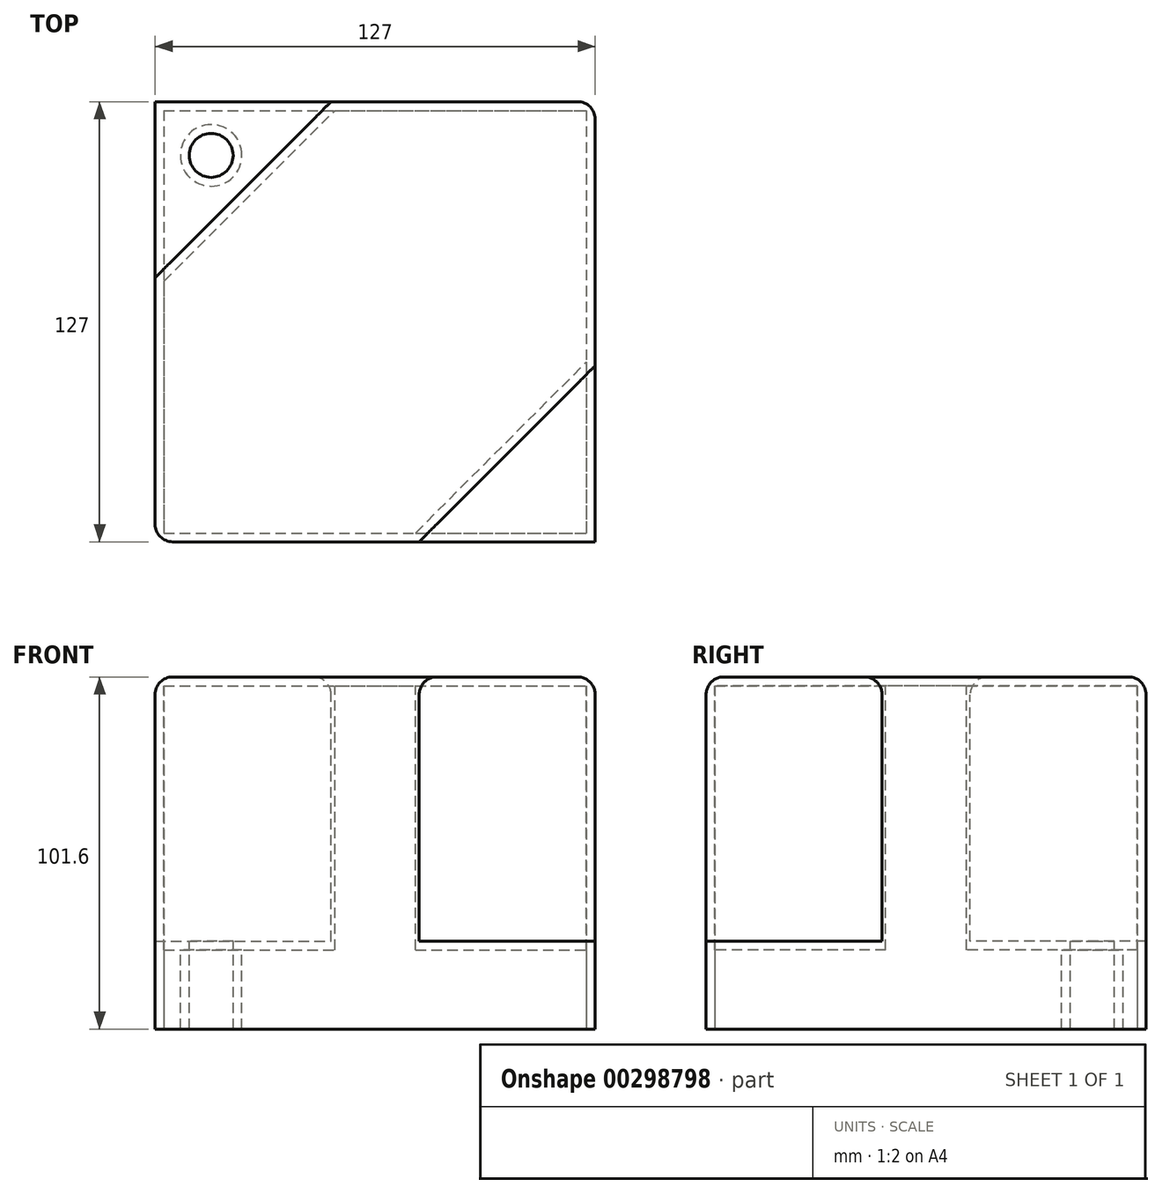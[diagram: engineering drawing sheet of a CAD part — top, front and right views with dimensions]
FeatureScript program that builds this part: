
annotation { "Feature Type Name" : "Feature", "Feature Type Description" : "" }
export const myFeature = defineFeature(function(context is Context, id is Id, definition is map)
    precondition{}
    {
        {
            var Q0;
            Q0=qCreatedBy(makeId("Top.planeOp"),FACE);
            var sketch = newSketch(context, id + "F0", { "sketchPlane" : qUnion([Q0])});
            skLineSegment(sketch, "E0.bottom", {"start": v(-63.5, 63.5) * mm, "end": v(63.5, 63.5) * mm});
            skLineSegment(sketch, "E0.top", {"start": v(-63.5, -63.5) * mm, "end": v(63.5, -63.5) * mm});
            skLineSegment(sketch, "E0.left", {"start": v(-63.5, 63.5) * mm, "end": v(-63.5, -63.5) * mm});
            skLineSegment(sketch, "E0.right", {"start": v(63.5, 63.5) * mm, "end": v(63.5, -63.5) * mm});
            skPoint(sketch, "E0.middle", {"position": v(0, 0) * mm});
            skSolve(sketch);
        }
        {
            var Q0;
            Q0=makeQuery(id+"F0.imprint","IMPRINT",FACE,{"disambiguationData":[TD([[makeQuery(id+"F0.imprint","IMPRINT",EDGE,{"derivedFrom":sQuery(id+"F0.wireOp",EDGE,"E0.bottom")}),-1.0]])]});
            extrude(context, id + "F1", {"entities" : qUnion([Q0]), "depth" : 101.6 * mm});
        }
        {
            var Q0;
            Q0=makeQuery(id+"F1.opExtrude","CAP_FACE",FACE,{"disambiguationData":[OSD([sQuery(id+"F0.wireOp",EDGE,"E0.bottom"),sQuery(id+"F0.wireOp",EDGE,"E0.top"),sQuery(id+"F0.wireOp",EDGE,"E0.left"),sQuery(id+"F0.wireOp",EDGE,"E0.right")])],"isStart":false});
            var sketch = newSketch(context, id + "F2", { "sketchPlane" : qUnion([Q0])});
            skLineSegment(sketch, "E1", {"start": v(-12.7, 63.5) * mm, "end": v(-63.5, 63.5) * mm});
            skLineSegment(sketch, "E2", {"start": v(-63.5, 63.5) * mm, "end": v(-63.5, 12.7) * mm});
            skLineSegment(sketch, "E3", {"start": v(-63.5, 12.7) * mm, "end": v(-12.7, 63.5) * mm});
            skLineSegment(sketch, "E4", {"start": v(-63.5, -63.5) * mm, "end": v(63.5, 63.5) * mm, "construction": true});
            skLineSegment(sketch, "E5.MirrorCS", {"start": v(12.7, -63.5) * mm, "end": v(63.5, -12.7) * mm});
            skLineSegment(sketch, "E6.MirrorCS", {"start": v(63.5, -12.7) * mm, "end": v(63.5, -63.5) * mm});
            skLineSegment(sketch, "E7.MirrorCS", {"start": v(63.5, -63.5) * mm, "end": v(12.7, -63.5) * mm});
            skSolve(sketch);
        }
        {
            var Q0;
            Q0=makeQuery(id+"F2.imprint","IMPRINT",FACE,{"disambiguationData":[TD([[makeQuery(id+"F2.imprint","IMPRINT",EDGE,{"derivedFrom":sQuery(id+"F2.wireOp",EDGE,"E5.MirrorCS")}),-1.0]])]});
            var Q1;
            Q1=makeQuery(id+"F2.imprint","IMPRINT",FACE,{"disambiguationData":[TD([[makeQuery(id+"F2.imprint","IMPRINT",EDGE,{"derivedFrom":sQuery(id+"F2.wireOp",EDGE,"E1")}),-1.0]])]});
            extrude(context, id + "F3", {"entities" : qUnion([Q0, Q1]), "operationType" : NewBodyOperationType.REMOVE, "oppositeDirection" : true, "depth" : 76.2 * mm});
        }
        {
            var Q0;
            Q0=makeQuery(id+"F3.boolean.opBoolean","COPY",FACE,{"derivedFrom":makeQuery(id+"F3.opExtrude","CAP_FACE",FACE,{"disambiguationData":[OSD([sQuery(id+"F2.wireOp",EDGE,"E1"),sQuery(id+"F2.wireOp",EDGE,"E2"),sQuery(id+"F2.wireOp",EDGE,"E3")])],"isStart":false})});
            var sketch = newSketch(context, id + "F4", { "sketchPlane" : qUnion([Q0])});
            skCircle(sketch, "E8", {"center": v(-47.34, 48) * mm, "radius": 6.35 * mm});
            skLineSegment(sketch, "E9", {"start": v(-63.56, -63.56) * mm, "end": v(63.34, 63.56) * mm, "construction": true});
            skCircle(sketch, "E10.MirrorC", {"center": v(47.98, -47.14) * mm, "radius": 6.35 * mm});
            skSolve(sketch);
        }
        {
            var Q0;
            Q0=makeQuery(id+"F4.imprint","IMPRINT",FACE,{"disambiguationData":[TD([[makeQuery(id+"F4.imprint","IMPRINT",EDGE,{"derivedFrom":sQuery(id+"F4.wireOp",EDGE,"E8")}),1.0]])]});
            var Q1;
            Q1=makeQuery(id+"F4.imprint","IMPRINT",FACE,{"disambiguationData":[TD([[makeQuery(id+"F4.imprint","IMPRINT",EDGE,{"derivedFrom":sQuery(id+"F4.wireOp",EDGE,"E10.MirrorC")}),-1.0]])]});
            extrude(context, id + "F5", {"entities" : qUnion([Q0, Q1]), "operationType" : NewBodyOperationType.REMOVE, "oppositeDirection" : true, "depth" : 203.2 * mm});
        }
        {
            var Q0;
            Q0=makeQuery(id+"F1.opExtrude","CAP_FACE",FACE,{"disambiguationData":[OSD([sQuery(id+"F0.wireOp",EDGE,"E0.bottom"),sQuery(id+"F0.wireOp",EDGE,"E0.top"),sQuery(id+"F0.wireOp",EDGE,"E0.left"),sQuery(id+"F0.wireOp",EDGE,"E0.right")])],"isStart":true});
            shell(context, id + "F6", {"entities" : qUnion([Q0]), "thickness" : 2.54 * mm});
        }
        {
            var Q0;
            Q0=makeQuery(id+"F3.boolean.opBoolean","COPY",EDGE,{"derivedFrom":makeQuery(id+"F3.opExtrude","CAP_EDGE",EDGE,{"disambiguationData":[OSD([sQuery(id+"F2.wireOp",EDGE,"E3")])],"isStart":true})});
            var Q1;
            Q1=makeQuery(id+"F1.opExtrude","CAP_EDGE",EDGE,{"disambiguationData":[OSD([sQuery(id+"F0.wireOp",EDGE,"E0.left")])],"isStart":false});
            var Q2;
            Q2=makeQuery(id+"F3.boolean.opBoolean","COPY",EDGE,{"derivedFrom":makeQuery(id+"F3.opExtrude","SWEPT_EDGE",EDGE,{"disambiguationData":[OSD([sQuery(id+"F0.wireOp",EDGE,"E0.left"),sQuery(id+"F2.wireOp",EDGE,"E2"),sQuery(id+"F2.wireOp",EDGE,"E3")])]})});
            var Q3;
            Q3=makeQuery(id+"F1.opExtrude","CAP_EDGE",EDGE,{"disambiguationData":[OSD([sQuery(id+"F0.wireOp",EDGE,"E0.bottom")])],"isStart":false});
            var Q4;
            Q4=makeQuery(id+"F1.opExtrude","CAP_EDGE",EDGE,{"disambiguationData":[OSD([sQuery(id+"F0.wireOp",EDGE,"E0.right")])],"isStart":false});
            var Q5;
            Q5=makeQuery(id+"F3.boolean.opBoolean","COPY",EDGE,{"derivedFrom":makeQuery(id+"F3.opExtrude","CAP_EDGE",EDGE,{"disambiguationData":[OSD([sQuery(id+"F2.wireOp",EDGE,"E5.MirrorCS")])],"isStart":true})});
            var Q6;
            Q6=makeQuery(id+"F3.boolean.opBoolean","COPY",EDGE,{"derivedFrom":makeQuery(id+"F3.opExtrude","SWEPT_EDGE",EDGE,{"disambiguationData":[OSD([sQuery(id+"F0.wireOp",EDGE,"E0.right"),sQuery(id+"F2.wireOp",EDGE,"E5.MirrorCS"),sQuery(id+"F2.wireOp",EDGE,"E6.MirrorCS")])]})});
            var Q7;
            Q7=makeQuery(id+"F3.boolean.opBoolean","COPY",EDGE,{"derivedFrom":makeQuery(id+"F3.opExtrude","SWEPT_EDGE",EDGE,{"disambiguationData":[OSD([sQuery(id+"F0.wireOp",EDGE,"E0.top"),sQuery(id+"F2.wireOp",EDGE,"E5.MirrorCS"),sQuery(id+"F2.wireOp",EDGE,"E7.MirrorCS")])]})});
            var Q8;
            Q8=makeQuery(id+"F1.opExtrude","CAP_EDGE",EDGE,{"disambiguationData":[OSD([sQuery(id+"F0.wireOp",EDGE,"E0.top")])],"isStart":false});
            var Q9;
            Q9=makeQuery(id+"F3.boolean.opBoolean","COPY",EDGE,{"derivedFrom":makeQuery(id+"F3.opExtrude","CAP_EDGE",EDGE,{"disambiguationData":[OSD([sQuery(id+"F2.wireOp",EDGE,"E6.MirrorCS")])],"isStart":false})});
            var Q10;
            Q10=makeQuery(id+"F3.boolean.opBoolean","COPY",EDGE,{"derivedFrom":makeQuery(id+"F3.opExtrude","CAP_EDGE",EDGE,{"disambiguationData":[OSD([sQuery(id+"F2.wireOp",EDGE,"E7.MirrorCS")])],"isStart":false})});
            var Q11;
            Q11=makeQuery(id+"F1.opExtrude","SWEPT_EDGE",EDGE,{"disambiguationData":[OSD([sQuery(id+"F0.wireOp",EDGE,"E0.bottom"),sQuery(id+"F0.wireOp",EDGE,"E0.right")])]});
            var Q12;
            Q12=makeQuery(id+"F3.boolean.opBoolean","COPY",EDGE,{"derivedFrom":makeQuery(id+"F3.opExtrude","SWEPT_EDGE",EDGE,{"disambiguationData":[OSD([sQuery(id+"F0.wireOp",EDGE,"E0.bottom"),sQuery(id+"F2.wireOp",EDGE,"E1"),sQuery(id+"F2.wireOp",EDGE,"E3")])]})});
            var Q13;
            Q13=makeQuery(id+"F3.boolean.opBoolean","COPY",EDGE,{"derivedFrom":makeQuery(id+"F3.opExtrude","CAP_EDGE",EDGE,{"disambiguationData":[OSD([sQuery(id+"F2.wireOp",EDGE,"E1")])],"isStart":false})});
            var Q14;
            Q14=makeQuery(id+"F3.boolean.opBoolean","COPY",EDGE,{"derivedFrom":makeQuery(id+"F3.opExtrude","CAP_EDGE",EDGE,{"disambiguationData":[OSD([sQuery(id+"F2.wireOp",EDGE,"E2")])],"isStart":false})});
            var Q15;
            Q15=makeQuery(id+"F1.opExtrude","SWEPT_EDGE",EDGE,{"disambiguationData":[OSD([sQuery(id+"F0.wireOp",EDGE,"E0.top"),sQuery(id+"F0.wireOp",EDGE,"E0.left")])]});
            fillet(context, id + "F7", {"entities" : qUnion([Q0, Q1, Q2, Q3, Q4, Q5, Q6, Q7, Q8, Q9, Q10, Q11, Q12, Q13, Q14, Q15]), "radius" : 5.08 * mm, "tangentPropagation" : true, "allowEdgeOverflow" : false});
        }
    });
